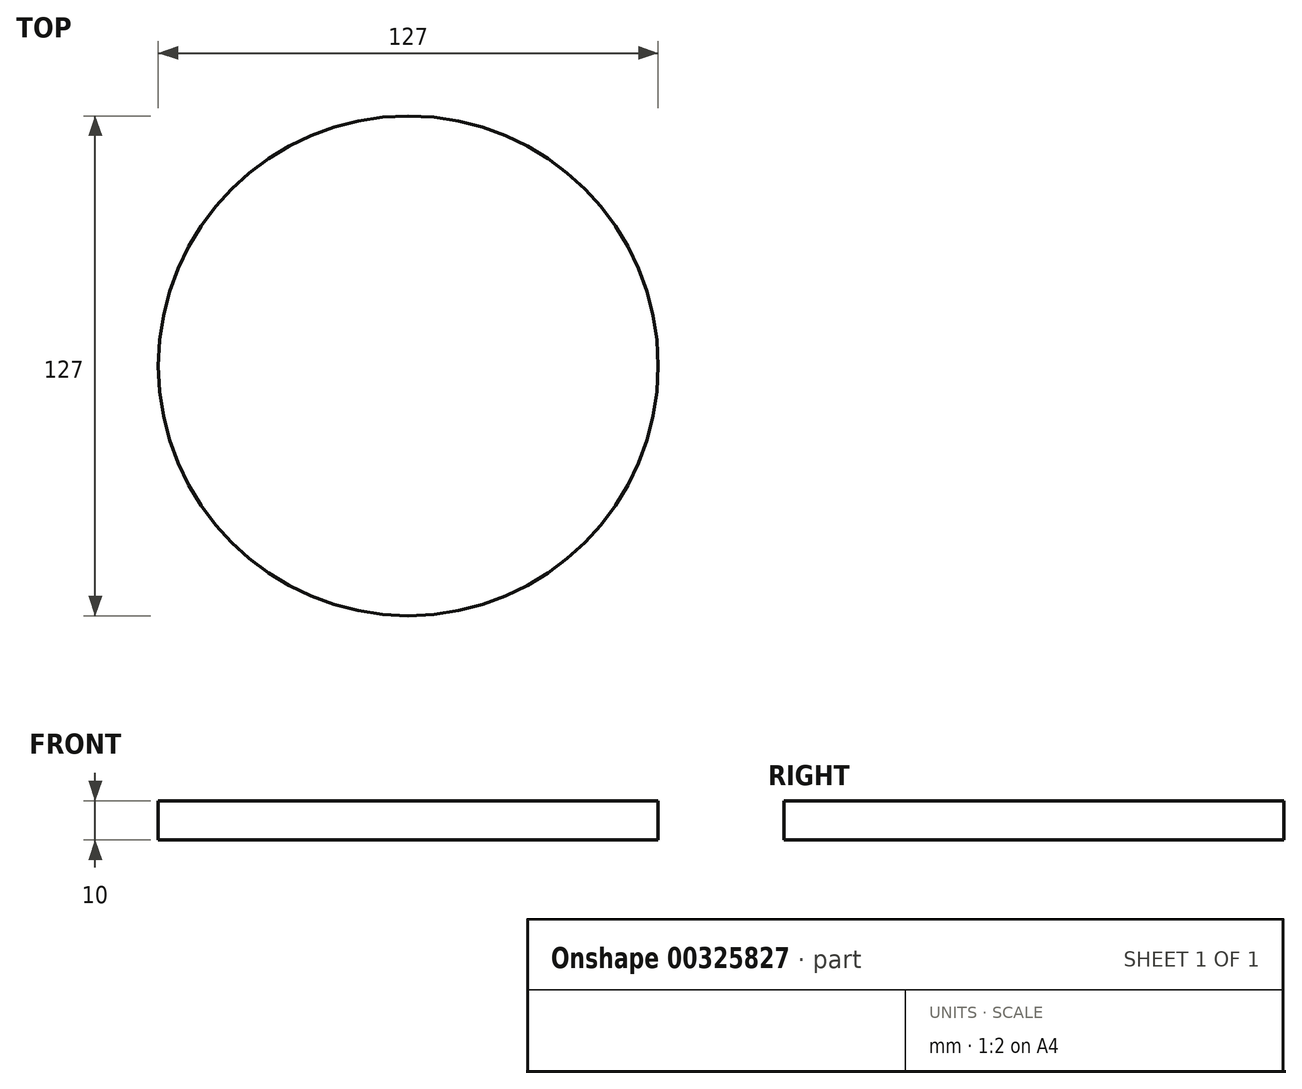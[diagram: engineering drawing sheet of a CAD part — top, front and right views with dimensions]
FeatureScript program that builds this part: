
annotation { "Feature Type Name" : "Feature", "Feature Type Description" : "" }
export const myFeature = defineFeature(function(context is Context, id is Id, definition is map)
    precondition{}
    {
        {
            var Q0;
            Q0=qCreatedBy(makeId("Top.planeOp"),FACE);
            var sketch = newSketch(context, id + "F0", { "sketchPlane" : qUnion([Q0])});
            skCircle(sketch, "E0", {"center": v(0, 0) * mm, "radius": 63.5 * mm});
            skSolve(sketch);
        }
        {
            var Q0;
            Q0=makeQuery(id+"F0.imprint","IMPRINT",FACE,{"disambiguationData":[TD([[makeQuery(id+"F0.imprint","IMPRINT",EDGE,{"derivedFrom":sQuery(id+"F0.wireOp",EDGE,"E0")}),1.0]])]});
            extrude(context, id + "F1", {"entities" : qUnion([Q0]), "depth" : 10 * mm});
        }
    });
